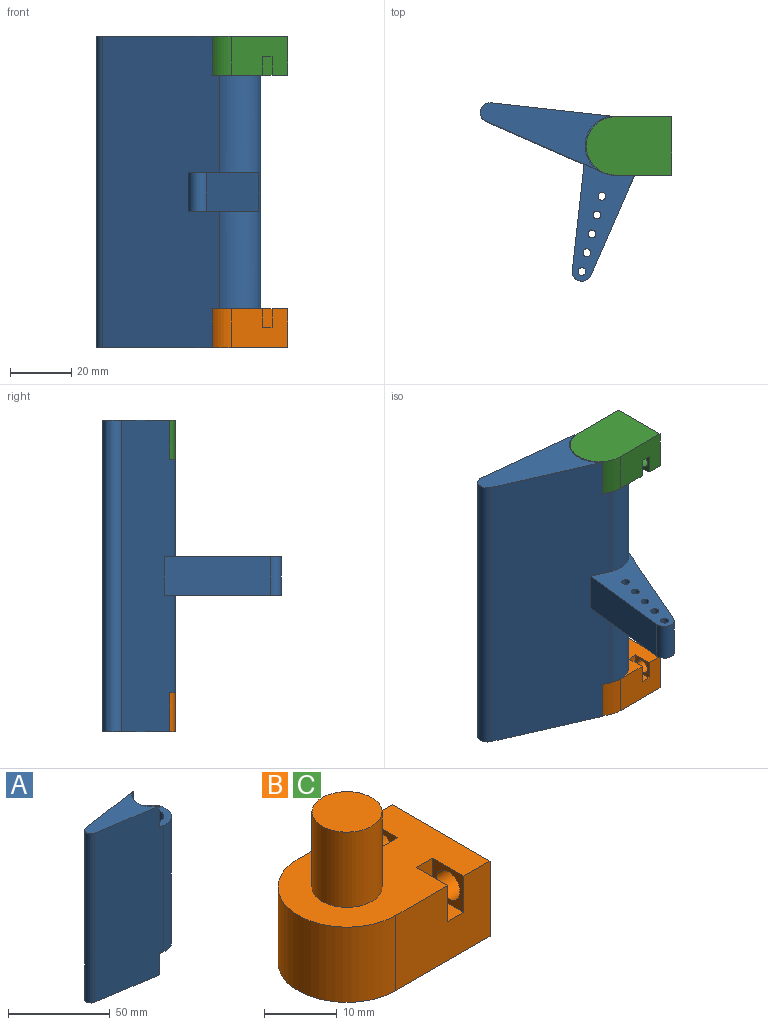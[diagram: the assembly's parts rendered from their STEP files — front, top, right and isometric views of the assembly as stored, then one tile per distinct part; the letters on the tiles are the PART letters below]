
ASSEMBLY  parts=3 mates=3
PART A: 21 faces, bbox 55x55x101.6 mm
  f0: cylinder r=9.91mm len=18.02mm, axis (0,0,-1), area 287.3mm2, adj f10,f13,f14,f17
  f1: plane 34.44x12.7mm, normal (-0.99,0.15,0), area 442.5mm2, adj f3,f14,f19,f20
  f2: plane 41.38x12.7mm, normal (0.99,0.15,0), area 531.6mm2, adj f3,f11,f19,f20
  f3: cylinder r=3.17mm len=12.7mm, axis (0,0,-1), area 114.5mm2, adj f1,f2,f19,f20
  f4: cylinder r=1.27mm len=12.7mm, axis (0,0,-1), area 101.3mm2, adj f19,f20
  f5: cylinder r=1.27mm len=12.7mm, axis (0,0,-1), area 101.3mm2, adj f19,f20
  f6: cylinder r=1.27mm len=12.7mm, axis (0,0,-1), area 101.3mm2, adj f19,f20
  f7: cylinder r=1.27mm len=12.7mm, axis (0,0,-1), area 101.3mm2, adj f19,f20
  f8: cylinder r=1.27mm len=12.7mm, axis (0,0,-1), area 101.3mm2, adj f19,f20
  f9: cylinder r=9.91mm len=18.02mm, axis (0,0,-1), area 287.3mm2, adj f10,f14,f16,f18
  f10: plane 101.6x41.38mm, normal (-0.15,-0.99,0), area 4183.3mm2, adj f0,f9,f11,f13,f15,f16,f17,f18
  f11: cylinder r=9.53mm len=76.2mm, axis (0,0,-1), area 2308.7mm2, adj f2,f10,f14,f17,f18,f19,f20
  f12: cylinder r=5.71mm len=76.2mm, axis (0,0,-1), area 2736.2mm2, adj f17,f18
  f13: plane 41.39x18.02mm, normal (0,0,-1), area 407.9mm2, adj f0,f10,f14,f15
  f14: plane 101.6x41.38mm, normal (-0.15,0.99,0), area 4094.2mm2, adj f0,f1,f9,f11,f13,f15,f16,f17
  f15: cylinder r=3.17mm len=101.6mm, axis (0,0,-1), area 916.3mm2, adj f10,f13,f14,f16
  f16: plane 41.39x18.02mm, normal (0,0,1), area 407.9mm2, adj f9,f10,f14,f15
  f17: plane 19.43x19.05mm, normal (0,0,-1), area 191.5mm2, adj f0,f10,f11,f12,f14
  f18: plane 19.43x19.05mm, normal (0,0,1), area 191.5mm2, adj f9,f10,f11,f12,f14
  f19: plane 44.08x17.78mm, normal (0,0,1), area 382.5mm2, adj f1,f2,f3,f4,f5,f6,f7,f8
  f20: plane 44.08x17.78mm, normal (0,0,-1), area 382.5mm2, adj f1,f2,f3,f4,f5,f6,f7,f8
PART B: 18 faces, bbox 27.9x19.1x25.4 mm
  f0: plane 18.33x12.7mm, normal (0,1,0), area 213.5mm2, adj f1,f3,f4,f5,f8,f10,f11
  f1: plane 27.86x19.05mm, normal (0,0,1), area 379.8mm2, adj f0,f2,f3,f4,f6,f8,f9,f10
  f2: plane 18.33x12.7mm, normal (0,-1,0), area 213.5mm2, adj f1,f3,f4,f5,f12,f14,f15
  f3: plane 19.05x12.7mm, normal (1,0,0), area 209.1mm2, adj f0,f1,f2,f5,f16,f17
  f4: cylinder r=9.53mm len=19.05mm, axis (0,0,-1), area 380mm2, adj f0,f1,f2,f5
  f5: plane 27.86x19.05mm, normal (0,0,-1), area 491.7mm2, adj f0,f2,f3,f4
  f6: cylinder r=4.83mm len=12.7mm, axis (0,0,-1), area 385.1mm2, adj f1,f7
  f7: plane 9.65x9.65mm, normal (0,0,1), area 73.2mm2, adj f6
  f8: plane 6.1x6.1mm, normal (1,0,0), area 37.2mm2, adj f0,f1,f9,f11
  f9: plane 6.1x3.18mm, normal (0,1,0), area 19.4mm2, adj f1,f8,f10,f11
  f10: plane 6.1x6.1mm, normal (-1,0,0), area 20.7mm2, adj f0,f1,f9,f11,f17
  f11: plane 6.1x3.18mm, normal (0,0,1), area 19.4mm2, adj f0,f8,f9,f10
  f12: plane 6.1x6.1mm, normal (-1,0,0), area 20.7mm2, adj f1,f2,f13,f15,f16
  f13: plane 6.1x3.18mm, normal (0,-1,0), area 19.4mm2, adj f1,f12,f14,f15
  f14: plane 6.1x6.1mm, normal (1,0,0), area 37.2mm2, adj f1,f2,f13,f15
  f15: plane 6.1x3.18mm, normal (0,0,1), area 19.4mm2, adj f2,f12,f13,f14
  f16: cylinder r=2.29mm len=5.08mm, axis (1,0,0), area 73mm2, adj f3,f12
  f17: cylinder r=2.29mm len=5.08mm, axis (1,0,0), area 73mm2, adj f3,f10
PART C: same geometry as B
PLACE A rot(axis=(0.99,-0.13,0),180deg) t=(-29.12,-61.91,112.85)mm
PLACE B t=(-29.12,-61.91,11.25)mm
PLACE C rot(axis=(1,0,0),180deg) t=(-29.12,-61.91,112.85)mm fixed
MATE parallel B.f3 <-> C.f3  axis (1,0,0) through (-10.79,-61.91,17.08)mm
MATE revolute A.f12 <-> B.f6  axis (0,0,-1) through (-29.12,-61.91,23.95)mm
MATE revolute C.f6 <-> A.f12  axis (0,0,-1) through (-29.12,-61.91,100.15)mm
